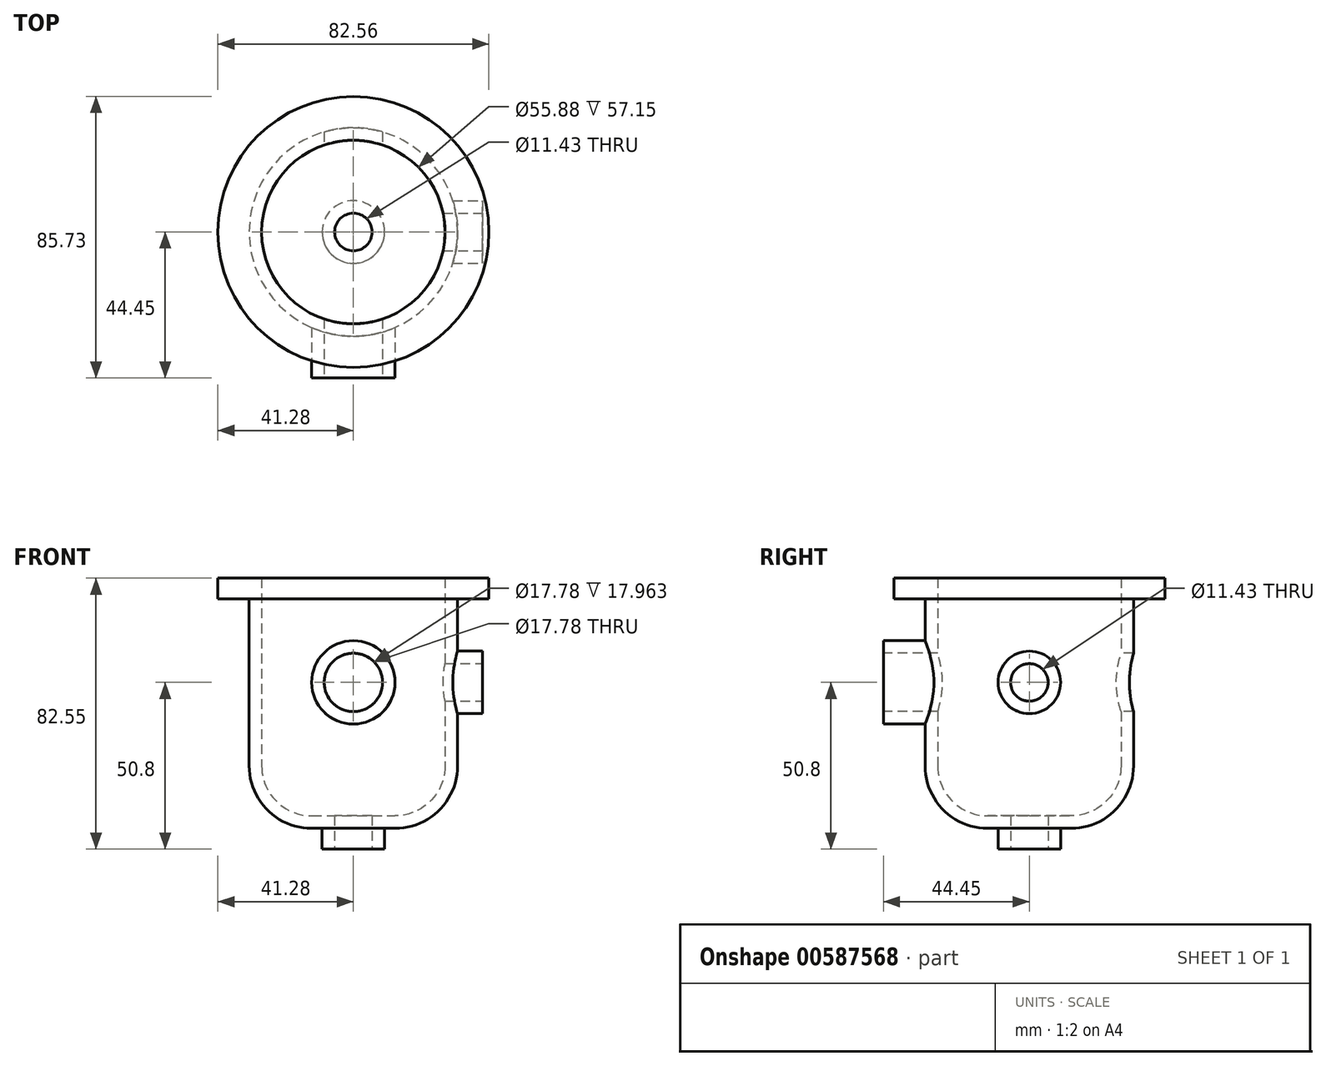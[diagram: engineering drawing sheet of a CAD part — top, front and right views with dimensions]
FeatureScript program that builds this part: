
annotation { "Feature Type Name" : "Feature", "Feature Type Description" : "" }
export const myFeature = defineFeature(function(context is Context, id is Id, definition is map)
    precondition{}
    {
        {
            var Q0;
            Q0=qCreatedBy(makeId("Front.planeOp"),FACE);
            var sketch = newSketch(context, id + "F0", { "sketchPlane" : qUnion([Q0])});
            skLineSegment(sketch, "E0", {"start": v(-41.28, 0) * mm, "end": v(-41.28, -6.35) * mm});
            skLineSegment(sketch, "E1", {"start": v(-41.28, -6.35) * mm, "end": v(-31.75, -6.35) * mm});
            skLineSegment(sketch, "E2", {"start": v(-31.75, -6.35) * mm, "end": v(-31.75, -57.15) * mm});
            skLineSegment(sketch, "E3", {"start": v(-12.7, -76.2) * mm, "end": v(0, -76.2) * mm});
            skPoint(sketch, "E4.visualSharp", {"position": v(-31.75, -76.2) * mm});
            skArc(sketch, "E4.filletArc", {"start": v(-31.75, -57.15) * mm, "mid": v(-26.17, -70.62) * mm, "end": v(-12.7, -76.2) * mm});
            skLineSegment(sketch, "E5", {"start": v(-27.94, 0) * mm, "end": v(-27.94, -57.15) * mm});
            skArc(sketch, "E6", {"start": v(-27.94, -57.15) * mm, "mid": v(-23.48, -67.93) * mm, "end": v(-12.7, -72.39) * mm});
            skLineSegment(sketch, "E7", {"start": v(-12.7, -72.39) * mm, "end": v(0, -72.39) * mm});
            skLineSegment(sketch, "E8", {"start": v(0, -76.2) * mm, "end": v(0, 0) * mm, "construction": true});
            skLineSegment(sketch, "E9", {"start": v(-41.28, 0) * mm, "end": v(-27.94, 0) * mm});
            skLineSegment(sketch, "E10", {"start": v(-27.94, 0) * mm, "end": v(0, 0) * mm, "construction": true});
            skLineSegment(sketch, "E11", {"start": v(0, -72.39) * mm, "end": v(0, -76.2) * mm});
            skSolve(sketch);
        }
        {
            var Q0;
            Q0 = qSketchRegion(id + "F0", true);
            var Q1;
            Q1=sQuery(id+"F0.wireOp",EDGE,"E8");
            revolve(context, id + "F1", {"entities" : qUnion([Q0]), "axis" : qUnion([Q1]), "revolveType" : RevolveType.FULL});
        }
        {
            var Q0;
            Q0 = qSketchRegion(id + "F0", true);
            var Q1;
            Q1=sQuery(id+"F0.wireOp",EDGE,"E8");
            revolve(context, id + "F2", {"entities" : qUnion([Q0]), "axis" : qUnion([Q1]), "revolveType" : RevolveType.FULL});
        }
        {
            var Q0;
            Q0=makeQuery(id+"F2.opRevolve","SWEPT_FACE",FACE,{"disambiguationData":[OSD([sQuery(id+"F0.wireOp",EDGE,"E3")])]});
            var sketch = newSketch(context, id + "F3", { "sketchPlane" : qUnion([Q0])});
            skCircle(sketch, "E12", {"center": v(0, 0) * mm, "radius": 9.53 * mm});
            skSolve(sketch);
        }
        {
            var Q0;
            Q0 = qSketchRegion(id + "F3", true);
            extrude(context, id + "F4", {"entities" : qUnion([Q0]), "operationType" : NewBodyOperationType.ADD, "depth" : 6.35 * mm, "offsetDistance" : 25.4 * mm});
        }
        {
            var Q0;
            Q0=qCreatedBy(makeId("Front.planeOp"),FACE);
            cPlane(context, id + "F5", {"entities" : qUnion([Q0]), "cplaneType" : CPlaneType.OFFSET, "offset" : 44.45 * mm, "width" : 152.4 * mm, "height" : 152.4 * mm});
        }
        {
            var Q0;
            Q0=qCreatedBy(id+"F5.planeOp",FACE);
            var sketch = newSketch(context, id + "F6", { "sketchPlane" : qUnion([Q0])});
            skCircle(sketch, "E13", {"center": v(0, -31.75) * mm, "radius": 12.7 * mm});
            skSolve(sketch);
        }
        {
            var Q0;
            Q0 = qSketchRegion(id + "F6", true);
            extrude(context, id + "F7", {"entities" : qUnion([Q0]), "operationType" : NewBodyOperationType.ADD, "endBound" : BoundingType.UP_TO_NEXT, "oppositeDirection" : true, "depth" : 25.4 * mm, "offsetDistance" : 25.4 * mm});
        }
        {
            var Q0;
            Q0=makeQuery(id+"F7.opExtrude","CAP_FACE",FACE,{"disambiguationData":[OSD([sQuery(id+"F6.wireOp",EDGE,"E13")])],"isStart":true});
            var sketch = newSketch(context, id + "F8", { "sketchPlane" : qUnion([Q0])});
            skCircle(sketch, "E14", {"center": v(0, -31.75) * mm, "radius": 8.9 * mm});
            skSolve(sketch);
        }
        {
            var Q0;
            Q0 = qSketchRegion(id + "F8", true);
            extrude(context, id + "F9", {"entities" : qUnion([Q0]), "operationType" : NewBodyOperationType.REMOVE, "oppositeDirection" : true, "depth" : 101.6 * mm, "offsetDistance" : 25.4 * mm});
        }
        {
            var Q0;
            Q0=makeQuery(id+"F4.opExtrude","CAP_FACE",FACE,{"disambiguationData":[OSD([sQuery(id+"F3.wireOp",EDGE,"E12")])],"isStart":false});
            var sketch = newSketch(context, id + "F10", { "sketchPlane" : qUnion([Q0])});
            skCircle(sketch, "E15", {"center": v(0, 0) * mm, "radius": 5.72 * mm});
            skSolve(sketch);
        }
        {
            var Q0;
            Q0 = qSketchRegion(id + "F10", true);
            extrude(context, id + "F11", {"entities" : qUnion([Q0]), "operationType" : NewBodyOperationType.REMOVE, "oppositeDirection" : true, "depth" : 25.4 * mm, "offsetDistance" : 25.4 * mm});
        }
        {
            var Q0;
            Q0=qCreatedBy(makeId("Right.planeOp"),FACE);
            cPlane(context, id + "F12", {"entities" : qUnion([Q0]), "cplaneType" : CPlaneType.OFFSET, "offset" : 39.37 * mm, "width" : 152.4 * mm, "height" : 152.4 * mm});
        }
        {
            var Q0;
            Q0=qCreatedBy(id+"F12.planeOp",FACE);
            var sketch = newSketch(context, id + "F13", { "sketchPlane" : qUnion([Q0])});
            skCircle(sketch, "E16", {"center": v(0, -31.75) * mm, "radius": 9.53 * mm});
            skSolve(sketch);
        }
        {
            var Q0;
            Q0=makeQuery(id+"F13.imprint","IMPRINT",FACE,{"disambiguationData":[TD([[makeQuery(id+"F13.imprint","IMPRINT",EDGE,{"derivedFrom":sQuery(id+"F13.wireOp",EDGE,"E16")}),1.0]])]});
            extrude(context, id + "F14", {"entities" : qUnion([Q0]), "operationType" : NewBodyOperationType.ADD, "endBound" : BoundingType.UP_TO_NEXT, "oppositeDirection" : true, "depth" : 25.4 * mm, "offsetDistance" : 25.4 * mm});
        }
        {
            var Q0;
            Q0=makeQuery(id+"F14.opExtrude","CAP_FACE",FACE,{"disambiguationData":[OSD([sQuery(id+"F13.wireOp",EDGE,"E16")])],"isStart":true});
            var sketch = newSketch(context, id + "F15", { "sketchPlane" : qUnion([Q0])});
            skCircle(sketch, "E17", {"center": v(0, -31.75) * mm, "radius": 5.72 * mm});
            skSolve(sketch);
        }
        {
            var Q0;
            Q0=makeQuery(id+"F15.imprint","IMPRINT",FACE,{"disambiguationData":[TD([[makeQuery(id+"F15.imprint","IMPRINT",EDGE,{"derivedFrom":sQuery(id+"F15.wireOp",EDGE,"E17")}),1.0]])]});
            extrude(context, id + "F16", {"entities" : qUnion([Q0]), "operationType" : NewBodyOperationType.REMOVE, "oppositeDirection" : true, "depth" : 25.4 * mm, "offsetDistance" : 25.4 * mm});
        }
    });
